# Revit family: Sink-Lavatory-KOHLER-Caxton_Oval-K-2205
name_source: partatom
category: Plumbing Fixtures
revit_build: Autodesk Revit 2015 (Build: 20140606_1530(x64)
units: mm (PartAtom-declared; Revit-internal decimal feet)

## types (6) — shared parameters
ADA Compliant = Yes
Assembly Code = D2010400
CW Connection = No
Cold Water Inlet = Cold Water Inlet
Date Modified = 10/01/2018
Default Elevation = 0"
Drain Included = No
HW Connection = No
Height = 8 1/4"
Hot Water Inlet = Hot Water Inlet
Length = 19 1/4"
Manufacturer = KOHLER Co.
MasterFormat 1995 = 15410
MasterFormat 2004 = 22.41.16
Material = Vitreous China
Product Documentation Link = http://www.us.kohler.com
Product Name = Caxton Oval
Product Page URL = http://www.us.kohler.com
URL = https://www.us.kohler.com
Vent Connection = No
Waste Connection = Yes
Waste Water Outlet = Waste Water Outlet
Width = 16 1/8"

## per-type parameters (varying)
| type | Description | Finish | Glazed Underside | Model | Type |
| 0-White | 17inches x 14inches under-mount bathroom sink with center drain and clamp assembly | Kohler-Vitreous_China-0-White | No | K-2205-0 | 1 |
| 96-Biscuit | 17inches x 14inches under-mount bathroom sink with center drain and clamp assembly | Kohler-Vitreous_China-96-Biscuit | No | K-2205-96 | 2 |
| 47-Almond | 17inches x 14inches under-mount bathroom sink with center drain and clamp assembly | Kohler-Vitreous_China-47-Almond | No | K-2205-47 | 3 |
| Glazed Underside, 0-White | 17inches x 14inches under-mount bathroom sink with center drain, glazed underside and clamp assembly | Kohler-Vitreous_China-0-White | Yes | K-2205-G-0 | 4 |
| Glazed Underside,96-Biscuit | 17inches x 14inches under-mount bathroom sink with center drain, glazed underside and clamp assembly | Kohler-Vitreous_China-96-Biscuit | Yes | K-2205-G-96 | 5 |
| Glazed Underside,47-Almond | 17inches x 14inches under-mount bathroom sink with center drain, glazed underside and clamp assembly | Kohler-Vitreous_China-47-Almond | Yes | K-2205-G-47 | 6 |

## geometry (parser evidence)
native form markers: Sweep x6
no freeform markers — native parametric forms only
